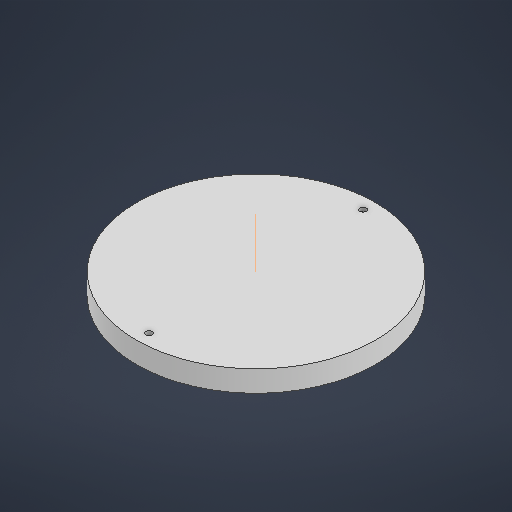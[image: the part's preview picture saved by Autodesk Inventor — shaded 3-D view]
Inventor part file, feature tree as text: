
AUTODESK INVENTOR PART (.ipt)
format: ipt  version: 2025 (Build 290162000, 162)  size: 192,000 bytes
history: native  units: in
note: dims shown in document units (in); Inventor stores cm internally (conversion verified against a paired STEP export)
features: extrude x3, sketch x2, other x1
ambient origin geometry x8: Origin, YZ Plane, XZ Plane, XY Plane, X Axis, Y Axis, Z Axis, Center Point
bodies: Solid1 (feature_tree)
feature tree (6):
  extrude  "Extrusion1"  Depth=0.5906in TaperAngle=0.0deg
  sketch  "Sketch2"  dims[d3=5.9843in d4=0.315in d5=0.315in d6=0.1772in d7=0.1772in d8=0.0in d9=0.0in d10=0.4724in d11=0.0in]
  extrude  "Extrusion2"  Depth=0.4724in
  extrude  "Extrusion3"  Depth=0.4724in
  other  "Work Axis1"
  sketch  "Sketch1"  dims[d0=6.6732in d1=0.5906in d2=0.0in]
